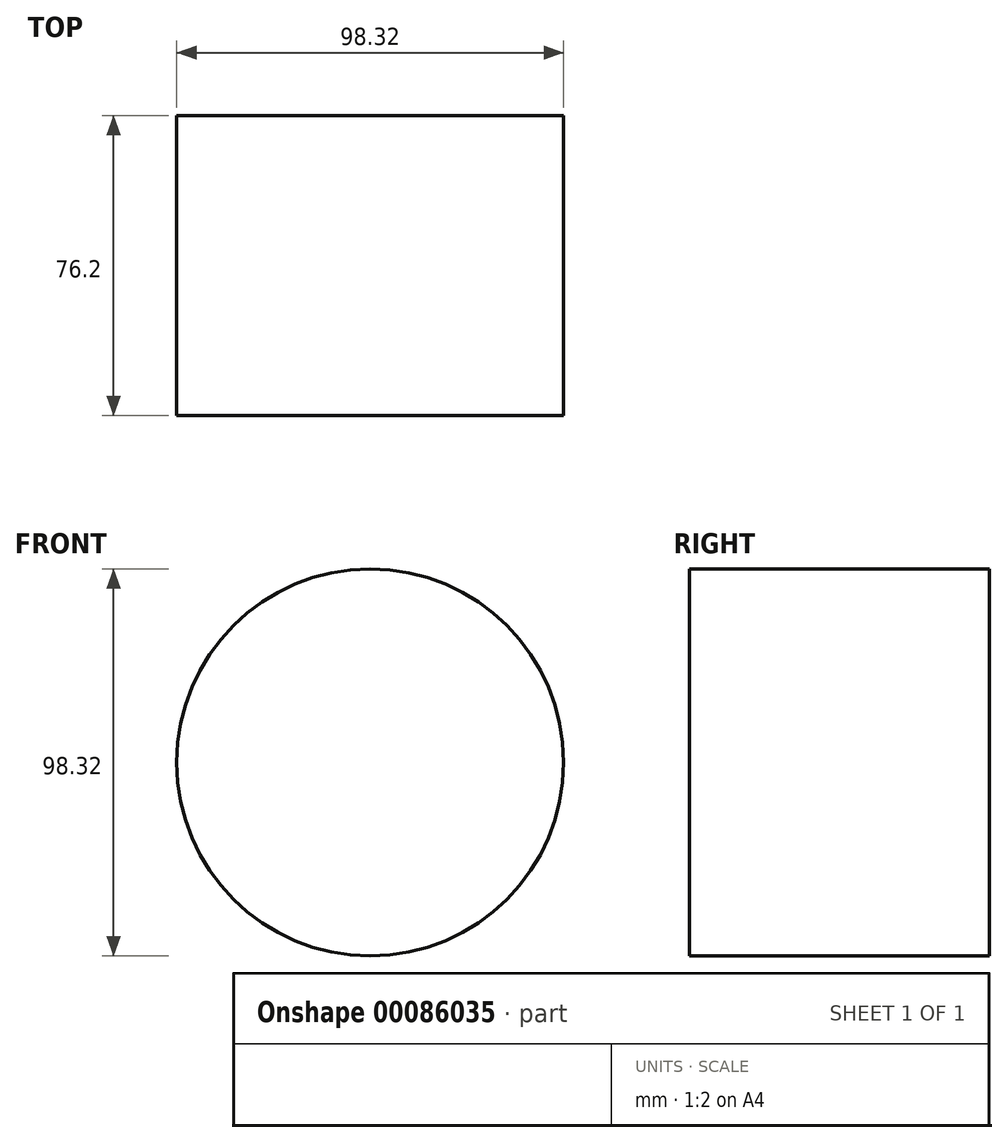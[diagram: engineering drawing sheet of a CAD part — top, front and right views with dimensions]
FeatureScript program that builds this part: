
annotation { "Feature Type Name" : "Feature", "Feature Type Description" : "" }
export const myFeature = defineFeature(function(context is Context, id is Id, definition is map)
    precondition{}
    {
        {
            var Q0;
            Q0=qCreatedBy(makeId("Front.planeOp"),FACE);
            var sketch = newSketch(context, id + "F0", { "sketchPlane" : qUnion([Q0])});
            skCircle(sketch, "E0", {"center": v(0, 0) * mm, "radius": 49.16 * mm});
            skSolve(sketch);
        }
        {
            var Q0;
            Q0=makeQuery(id+"F0.imprint","IMPRINT",FACE,{"disambiguationData":[TD([[makeQuery(id+"F0.imprint","IMPRINT",EDGE,{"derivedFrom":sQuery(id+"F0.wireOp",EDGE,"E0")}),1.0]])]});
            extrude(context, id + "F1", {"entities" : qUnion([Q0]), "depth" : 76.2 * mm});
        }
    });
